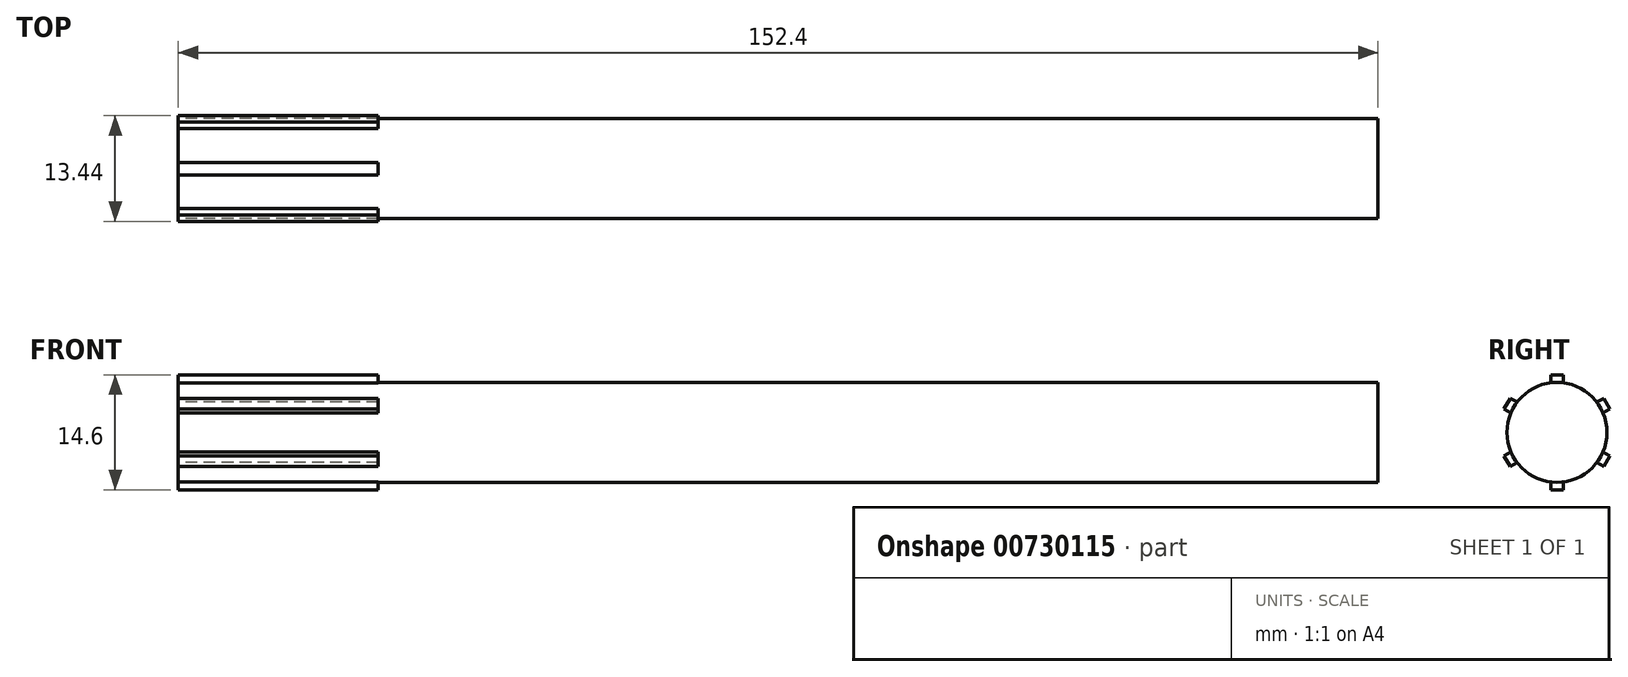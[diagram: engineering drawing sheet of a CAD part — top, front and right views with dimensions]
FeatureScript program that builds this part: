
annotation { "Feature Type Name" : "Feature", "Feature Type Description" : "" }
export const myFeature = defineFeature(function(context is Context, id is Id, definition is map)
    precondition{}
    {
        {
            var Q0;
            Q0=qCreatedBy(makeId("Top.planeOp"),FACE);
            var sketch = newSketch(context, id + "F0", { "sketchPlane" : qUnion([Q0])});
            skLineSegment(sketch, "E0", {"start": v(0, 0) * mm, "end": v(152.4, 0) * mm});
            skLineSegment(sketch, "E1", {"start": v(152.4, 0) * mm, "end": v(152.4, 6.35) * mm});
            skLineSegment(sketch, "E2", {"start": v(152.4, 6.35) * mm, "end": v(0, 6.35) * mm});
            skLineSegment(sketch, "E3", {"start": v(0, 6.35) * mm, "end": v(0, 0) * mm});
            skSolve(sketch);
        }
        {
            var Q0;
            Q0=makeQuery(id+"F0.imprint","IMPRINT",FACE,{"disambiguationData":[TD([[makeQuery(id+"F0.imprint","IMPRINT",EDGE,{"derivedFrom":sQuery(id+"F0.wireOp",EDGE,"E0")}),1.0]])]});
            var Q1;
            Q1=sQuery(id+"F0.wireOp",EDGE,"E0");
            revolve(context, id + "F1", {"surfaceOperationType" : NewSurfaceOperationType.NEW, "entities" : qUnion([Q0]), "axis" : qUnion([Q1]), "revolveType" : RevolveType.FULL});
        }
        {
            var Q0;
            Q0=makeQuery(id+"F1.opRevolve","SWEPT_FACE",FACE,{"disambiguationData":[OSD([sQuery(id+"F0.wireOp",EDGE,"E3")])]});
            var sketch = newSketch(context, id + "F2", { "sketchPlane" : qUnion([Q0])});
            skLineSegment(sketch, "E4.bottom", {"start": v(-0.8, 7.3) * mm, "end": v(0.8, 7.3) * mm});
            skLineSegment(sketch, "E4.top", {"start": v(-0.8, -7.3) * mm, "end": v(0.8, -7.3) * mm});
            skLineSegment(sketch, "E4.left", {"start": v(-0.8, 7.3) * mm, "end": v(-0.8, -7.3) * mm});
            skLineSegment(sketch, "E4.right", {"start": v(0.8, 7.3) * mm, "end": v(0.8, -7.3) * mm});
            skLineSegment(sketch, "E5", {"start": v(-0.8, 0) * mm, "end": v(0.8, 0) * mm, "construction": true});
            skSolve(sketch);
        }
        {
            var Q0;
            Q0 = qSketchRegion(id + "F2", true);
            extrude(context, id + "F3", {"entities" : qUnion([Q0]), "operationType" : NewBodyOperationType.ADD, "oppositeDirection" : true, "depth" : 25.4 * mm, "offsetDistance" : 25.4 * mm});
        }
        {
            var Q0;
            Q0=makeQuery(id+"F1.opRevolve","SWEPT_BODY",BODY,{"disambiguationData":[OSD([sQuery(id+"F0.wireOp",EDGE,"E0"),sQuery(id+"F0.wireOp",EDGE,"E1"),sQuery(id+"F0.wireOp",EDGE,"E2"),sQuery(id+"F0.wireOp",EDGE,"E3")])]});
            var Q1;
            Q1=makeQuery(id+"F1.opRevolve","SWEPT_FACE",FACE,{"disambiguationData":[OSD([sQuery(id+"F0.wireOp",EDGE,"E2")])]});
            circularPattern(context, id + "F4", {"operationType" : NewBodyOperationType.ADD, "entities" : qUnion([Q0]), "axis" : qUnion([Q1]), "angle" : 360 * degree, "instanceCount" : 6, "equalSpace" : true});
        }
    });
